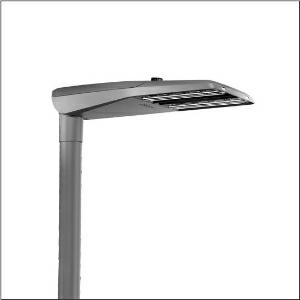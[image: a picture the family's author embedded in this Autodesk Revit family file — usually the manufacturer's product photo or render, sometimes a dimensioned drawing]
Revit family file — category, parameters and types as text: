
# Revit family: streetlight_sl_11_iq_midi___st1_2a_5xc3a51u08me_6b2b
name_source: partatom
category: Lighting Fixtures
units: mm (PartAtom-declared; Revit-internal decimal feet)

## family parameters
Cut with Voids When Loaded = No
Host = Face
Light Source = No
Part Type = Normal
Room Calculation Point = No
Round Connector Dimension = Use Diameter
Shared = No

## types (1)
- --- (1 x LED, 18110 lm, 122.7 W, 3000K)
    Apparent Load = 123 VA
    CIE Flux Codes = 32 70 96 100 100
    Color Rendering = 70
    Color Temperature = 3000K
    Default Elevation = 1800 mm
    Description = Streetlight SL 11 iQ midi, mast luminaire, primary light control with 3 zone facetted reflector, of plastic, silver coated, highly specular, primary optical cover: cover, of PMMA, transparent, light distribution: ST1.2a, light emission: direct distribution, primary light characteristic: asymmetric, installation type: post-top, side-entry, lamps: LED, High Power LED, rated values: 18.110lm | 122,7W | 147,6lm/W (begin service life); end service life: 18.110lm | 130,2W; at 50% lumin. flux: 9.055lm | 56,1W | 161,4lm/W, colour temperature: 3000K, colour rendering: CRI > 70, light colour: 730, light setting 1 begin service life: 100% | 18.110lm | 122,7W | 147,6lm/W | 3.000K, light setting 1 end service life: 130,2W, further light settings possible, control: pre-setting: logarithmic dimming characteristic, Street-Remote, Auto-Match, Temp-Guard, Lumen-Switch, Night-Set, Smart-Wire, Light-Fading, Desk-Remote (wireless, voltage-free reading and setting of iQ features in the workshop via application-optimized NFC function/RFID function), optimised constant luminous flux control (CLO 2.0), with cable H07RN-F 3x 1.5mm², mains connection: 230..240V, AC, 50/60Hz, connection cable pre-assembled, cable length: 12,5m, luminaire housing, of diecast aluminium, powder-coated, SITECO metallic grey (DB 702S), please order mast flange separately, inclination adjustable without tools: 0°, 5°, 10°, 15° (post-top) | 0°, -5°, -10°, -15° (side-entry), sealing non-destructively replaceable, multi-level sealing system, length: 780mm, width: 376mm, height: 118mm, mast flange for spigot size: 42mm (side-entry): 5XC10008XM4, 60/48mm (side-entry/post-top): 5XC10108XM2, 76/60mm (side-entry/post-top): 5XC10108XM1, equipment: Power, Smart Interface below, protection rating (complete): IP66, insulation class (complete): insulation class II (safety insulation), certification: CE, ENEC, ENEC+, VDE, UKCA, impact resistance: IK10, permissible operating ambient temperature for outdoor applications: -25..+50°C, standard-compliant lighting for roads and squares, Environmental Product Declaration (EPD) tested and certified by an independent institute, packaging unit: 1 piece

Light Distribution: ST1.2a
    Height = 118 mm
    Lamp = 1 x LED
    Lamp Light Flux = 18110 lm
    Lamp Power = 122.7 W
    Lamp count = 1
    Length = 780 mm
    Luminous efficacy = 148 lm/W
    Manufacturer = Siteco
    ModVariant = No
    Model = 5XC3A51U08ME
    Number of Poles = 1
    OnlyDefault = Yes
    Power Factor = 1
    Product Name = Streetlight SL 11 iQ midi | ST1.2a
    Product group = mast luminaire | pylon top
    ProductGroupID = 6100
    Protection Class = Protection class II
    Protection Degree = IP 66
    RLX_Detail_Level = 1
    RLX_Emergency_Light_Flux = 0 lm
    RLX_Emergency_Type = 0
    RLX_Emergency_Type_DB = No
    RlxData = <blob elided: 70081 chars, md5=26c84c9f>
    Socket = socket
    Standby Power = 0 W
    System Light Flux = 18111 lm
    System Power = 123 W
    Type Comments = factory setting: luminous flux: 100 % | dim-lin: 254 | 553 mA
    Type Image = l_1005968.jpg
    URL = http://relux.com
    VarID = @adj_132765
    Voltage = 0 V
    Weight = 0.00 kg
    Width = 376 mm

## geometry (parser evidence)
native form markers: Blend x4, Sweep x12
no freeform markers — native parametric forms only
